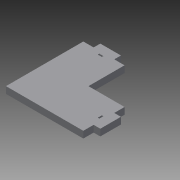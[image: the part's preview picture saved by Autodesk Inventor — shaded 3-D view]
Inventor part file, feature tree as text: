
AUTODESK INVENTOR PART (.ipt)
format: ipt  version: 2013 (Build 170138000, 138)  size: 107,520 bytes
history: native  units: mm
features: extrude x3, sketch x3
ambient origin geometry x8: Origin, YZ Plane, XZ Plane, XY Plane, X Axis, Y Axis, Z Axis, Center Point
bodies: Solid1 (feature_tree)
feature tree (6):
  extrude  "Extrusion1"  Depth=40.0mm
  extrude  "Extrusion2"  Depth=6.477mm
  extrude  "Extrusion3"  Depth=0.255mm TaperAngle=0.0deg
  sketch  "Sketch1"  dims[d0=75.0mm d2=40.0mm]
  sketch  "Sketch2"  dims[d3=6.477mm d4=0.0mm d5=6.477mm]
  sketch  "Sketch3"  dims[d7=20.0mm d8=0.255mm d9=0.0mm d10=2.5mm d11=2.5mm d12=1.5mm d13=4.0mm d14=0.255mm d15=0.0mm]
